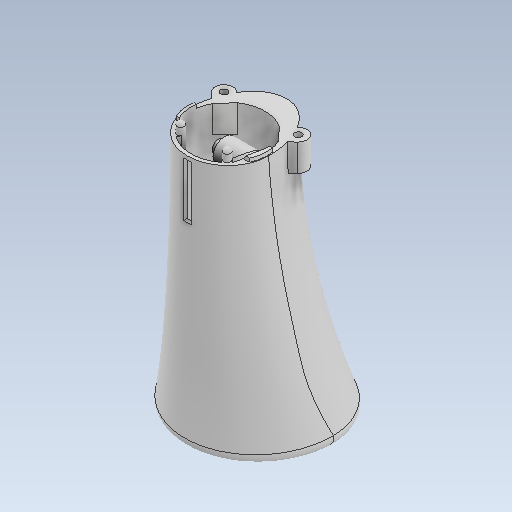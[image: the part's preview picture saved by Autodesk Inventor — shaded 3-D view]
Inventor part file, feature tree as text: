
AUTODESK INVENTOR PART (.ipt)
format: ipt  version: 2021 (Build 250183000, 183)  size: 964,608 bytes
history: native  units: mm
features: sketch x36, extrude x24, plane x15, fillet x6, hole x3, loft x2, revolve x2, other x1, thread x1
ambient origin geometry x8: Origin, YZ Plane, XZ Plane, XY Plane, X Axis, Y Axis, Z Axis, Center Point
bodies: Body1 (feature_tree)
feature tree (90):
  other  "Sólido1"
  plane  "Plano de trabajo1"
  plane  "Plano de trabajo2"
  plane  "Plano de trabajo4"
  plane  "Plano de trabajo5"
  plane  "Plano de trabajo6"
  sketch  "Boceto1"  dims[d1=250.0mm d2=0.0mm d3=-80.0mm d4=-110.0mm]
  sketch  "Boceto2"  dims[d5=-140.0mm d7=-0.0mm d8=2.0mm]
  sketch  "Boceto3"  dims[d9=140.0mm d10=250.0mm]
  sketch  "Boceto4"  dims[d11=24.0mm d22=0.0mm d23=90.0deg d24=0.0mm d25=90.0deg]
  sketch  "Boceto6"  dims[d44=45.0mm d49=29.11157mm]
  sketch  "Boceto7"  dims[d50=29.11157mm d53=29.11157mm]
  loft  "Solevación1"
  fillet  "Empalme2"  [1 undecoded]
  extrude  "Extrusión1"  TaperAngle=0.0deg  [1 undecoded]
  fillet  "Empalme5"  Radius=2.0mm
  plane  "Plano de trabajo7"
  extrude  "Extrusión2"  Depth=250.0mm
  plane  "Plano de trabajo8"
  plane  "Plano de trabajo9"
  loft  "Solevación9"
  plane  "Plano de trabajo10"
  extrude  "Extrusión3"  Depth=29.11157mm
  plane  "Plano de trabajo11"
  revolve  "Revolución1"  [1 undecoded]
  revolve  "Revolución2"  [1 undecoded]
  extrude  "Extrusión4"  Depth=32.5mm
  plane  "Plano de trabajo12"
  extrude  "Extrusión5"  Depth=44.747934mm
  plane  "Plano de trabajo13"
  plane  "Plano de trabajo14"
  extrude  "Extrusión6"  Depth=42.747934mm
  extrude  "Extrusión7"  Depth=42.747934mm
  extrude  "Extrusión8"  Depth=13.0mm
  extrude  "Extrusión11"  Depth=7.75mm
  extrude  "Extrusión9"  Depth=7.75mm
  extrude  "Extrusión10"  Depth=16.0mm
  extrude  "Extrusión12"  Depth=12.0mm
  sketch  "Boceto30"  dims[d160=-19.75mm d161=0.0mm d163=0.0mm d164=2.0mm]
  extrude  "Extrusión13"  Depth=7.75mm
  extrude  "Extrusión14"  Depth=7.75mm
  extrude  "Extrusión15"  TaperAngle=0.0deg  [1 undecoded]
  hole  "Agujero1"  [1 undecoded]
  thread  "Rosca1"  [1 undecoded]
  extrude  "Extrusión16"  Depth=2.0mm
  plane  "Plano de trabajo16"
  extrude  "Extrusión17"  TaperAngle=0.0deg  [1 undecoded]
  extrude  "Extrusión18"  TaperAngle=0.0deg  [1 undecoded]
  sketch  "Boceto45"  dims[d185=2.0mm]
  fillet  "Empalme6"  [1 undecoded]
  fillet  "Empalme7"  Radius=2.0mm
  extrude  "Extrusión19"  Depth=4.0mm
  extrude  "Extrusión20"  Depth=12.0mm
  plane  "Plano de trabajo17"
  sketch  "Boceto46"  dims[d187=1.0mm]
  hole  "Agujero2"  [1 undecoded]
  hole  "Agujero3"  [1 undecoded]
  extrude  "Extrusión21"  Depth=1.0mm
  sketch  "Boceto44"  dims[d181=0.75mm d182=0.25mm d183=1.0mm d184=0.25mm]
  sketch  "Boceto47"  dims[d189=3.0mm]
  sketch  "Boceto49"  dims[d191=2.0mm d192=0.25mm d193=0.25mm d194=90.0deg d196=4.381635mm d197=0.0mm d198=-48.35mm d199=12.0mm d200=20.0mm d201=9.0mm d202=9.0mm d203=2.0mm d204=201.65mm d205=0.0mm d206=0.5mm d207=0.25mm d208=-7.5mm d209=100.0mm d210=0.0mm d211=35.0mm d212=0.0mm d213=210.0mm d214=0.0mm d215=2.0mm d216=1.059493mm d217=6.5mm d218=1.059493mm d219=5.0mm d220=2.0mm d221=0.0mm d222=2.0mm d223=6.5mm d224=1.059493mm d225=5.0mm d226=4.85mm d227=2.0mm d228=0.0mm d229=6.0mm d230=10.0mm d231=3.0mm d232=11.0mm d233=10.5mm d235=30.0deg d236=4.75mm d237=0.0mm d238=-17.0mm d239=100.0mm d240=0.0mm d241=6.5mm d242=1.65mm d243=3.3mm d244=15.6mm d245=2.0mm d247=16.0mm d248=2.0mm d249=0.0mm d250=4.5mm d251=0.75mm d252=2.5mm d253=1.0mm d254=11.0mm d255=17.453293mm d256=2.939597mm d257=0.75mm d258=0.75mm d259=0.25mm d260=1.0mm d261=0.25mm d262=2.0mm d263=1.0mm d264=3.0mm d265=2.0mm d266=2.0mm d267=0.25mm d268=0.25mm d269=40.0mm d270=1.0mm d271=1.0mm d272=7.75mm d273=0.5mm d274=8.5mm d275=90.0deg d276=0.0mm d277=17.75mm d280=22.5mm d281=2.0mm d282=0.0mm d283=0.0mm d292=2.0mm d293=0.0mm d296=3.5mm d297=0.0mm d299=4.0mm d300=3.708mm d301=3.023mm d302=2.0mm d303=14.3117mm d304=16.0mm d305=0.0mm d306=16.0mm d307=0.0mm d314=6.0mm d315=19.2mm d316=6.0mm d317=19.2mm d318=13.0mm d320=6.0mm d321=19.2mm d322=13.0mm d323=6.0mm d324=19.2mm d325=13.0mm d326=7.0mm d332=10.0mm d333=0.0mm d335=-41.6mm d336=4.0mm d337=1.0mm d338=9.0mm d339=4.0mm d340=1.0mm d341=9.0mm d342=4.0mm d343=5.2mm d344=4.0mm d345=0.0mm d346=15.0mm d347=5.0mm d349=5.0mm d351=0.0mm d352=45.0mm d354=10.0mm d355=10.0mm d356=0.0mm d357=15.0mm d358=0.0mm d359=2.0mm d363=50.4125mm d376=14.159493mm d377=2.0mm d379=2.0mm d380=11.25mm d381=90.0mm d382=290.0mm d383=14.059493mm d384=100.825mm d390=30.940507mm d391=2.0mm d392=100.825mm d393=14.790546mm d394=2.0mm d395=3.0mm d396=6.0mm d397=4.0mm d398=4.0mm d399=4.0mm d400=8.128453mm d401=12.0mm d402=4.45mm d403=2.5mm d404=1.65mm d405=1.65mm d406=1.0mm d407=2.0mm d408=2.0mm d409=0.0mm d411=50.4125mm d412=6.0mm d413=0.0mm d414=0.0mm d415=0.0mm d416=0.0mm d418=13.059493mm d419=6.5mm d420=6.5mm d421=50.4125mm d422=126.03125mm d423=0.0mm d424=15.0mm d425=5.0mm d426=5.0mm d427=0.0mm d428=45.0mm d429=10.0mm d430=2.0mm d431=4.0mm d432=6.0mm d433=8.0mm d434=2.0mm d435=90.0deg d436=20.0mm d437=0.0mm d438=4.0mm d439=6.0mm d440=8.0mm d441=2.0mm d442=90.0deg d443=20.0mm d444=0.0mm d446=10.0mm d447=3.0mm d448=11.5mm d450=9.0mm d451=9.0mm d452=90.0mm d453=750.0mm d454=22.5mm d455=43.0mm d456=44.0mm d457=14.159493mm d458=11.25mm d459=2.0mm d460=0.0mm d461=22.5mm d462=43.0mm d463=7.059493mm d464=3.0mm d465=4.0mm d466=3.0mm d467=4.0mm d468=180.0mm d469=0.0mm d470=8.0mm d471=0.0mm d472=45.0mm d473=6.0mm d474=0.0mm d475=2.0mm d476=0.0mm d477=4.0mm]
  extrude  "Extrusión22"  Depth=17.453293mm
  extrude  "Extrusión23"  Depth=0.75mm
  extrude  "Extrusión24"  Depth=0.25mm
  fillet  "Empalme8"  Radius=1.0mm
  fillet  "Empalme9"  Radius=0.25mm
  sketch  "Boceto9"  dims[d59=29.11157mm d61=29.11157mm]
  sketch  "Boceto10"  dims[d65=22.5mm d66=32.5mm]
  sketch  "Boceto15"  dims[d67=22.5mm d90=44.747934mm]
  sketch  "Boceto16"  dims[d91=42.747934mm d93=42.747934mm]
  sketch  "Boceto17"  dims[d96=0.0mm d97=90.0deg d98=0.0mm d99=90.0deg d100=0.0mm d101=90.0deg d102=0.0mm d103=90.0deg d112=42.747934mm]
  sketch  "Boceto18"  dims[d115=5.0mm d120=13.0mm]
  sketch  "Boceto19"  dims[d121=6.5mm d124=7.75mm]
  sketch  "Boceto20"  dims[d125=7.75mm d126=7.75mm]
  sketch  "Boceto21"  dims[d127=7.75mm d130=16.0mm]
  sketch  "Boceto22"  dims[d131=0.0mm d132=12.0mm]
  sketch  "Boceto24"  dims[d133=12.0mm d134=7.75mm]
  sketch  "Boceto25"  dims[d135=6.5mm d136=7.75mm]
  sketch  "Boceto26"  dims[d137=15.0mm d138=0.0mm]
  sketch  "Boceto27"  dims[d146=-8.5mm d147=30.0mm d148=2.0mm]
  sketch  "Boceto28"  dims[d149=25.12mm d150=2.0mm]
  sketch  "Boceto29"  dims[d151=10.357mm d156=0.0mm d157=90.0deg d158=0.0mm d159=90.0deg]
  sketch  "Boceto31"  dims[d165=15.0mm d166=4.0mm]
  sketch  "Boceto36"  dims[d167=30.0mm d168=12.0mm]
  sketch  "Boceto37"  dims[d169=0.0mm d170=-7.25mm]
  sketch  "Boceto38"  dims[d171=4.5mm d172=0.75mm]
  sketch  "Boceto39"  dims[d173=2.5mm d174=1.0mm]
  sketch  "Boceto40"  dims[d176=11.0mm d177=17.453293mm]
  sketch  "Boceto41"  dims[d179=2.939597mm d180=0.75mm]
  sketch  "Boceto48"  dims[d190=2.0mm]
note: 12 required parameter values undecoded (feature->parameter linkage not recoverable at this tier; creation-order binding heuristic only, values carry confidence <= 0.55)